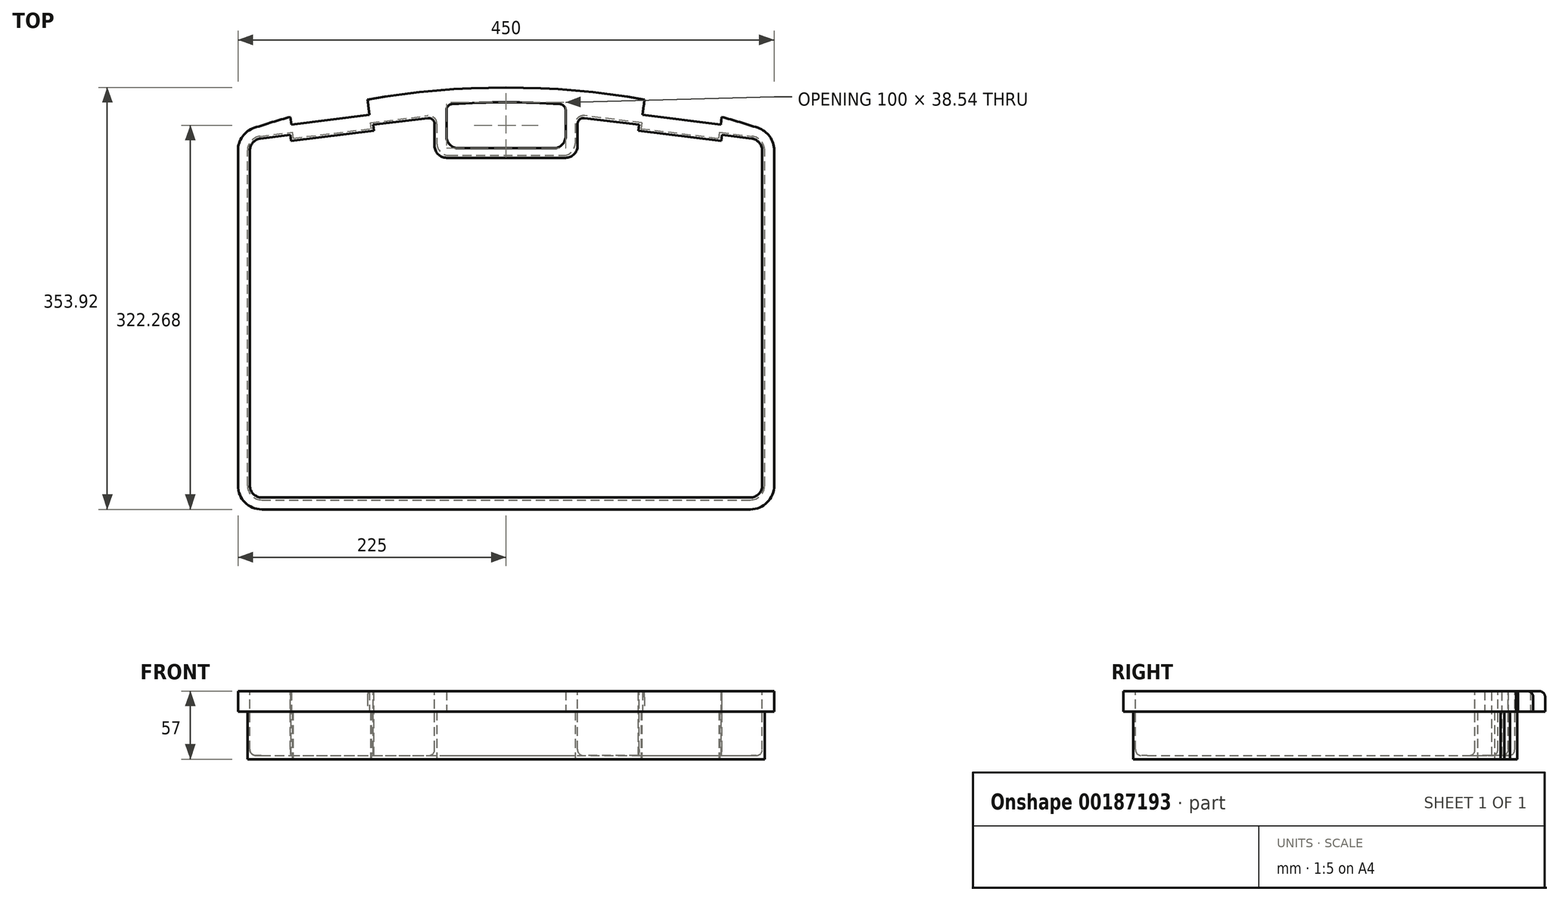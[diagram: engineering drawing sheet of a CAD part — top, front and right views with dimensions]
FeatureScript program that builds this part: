
annotation { "Feature Type Name" : "Feature", "Feature Type Description" : "" }
export const myFeature = defineFeature(function(context is Context, id is Id, definition is map)
    precondition{}
    {
        {
            var Q0;
            Q0=qCreatedBy(makeId("Top.planeOp"),FACE);
            var sketch = newSketch(context, id + "F0", { "sketchPlane" : qUnion([Q0])});
            skLineSegment(sketch, "E0.bottom", {"start": v(10, 0) * mm, "end": v(420, 0) * mm});
            skLineSegment(sketch, "E1.top", {"start": v(165, 285) * mm, "end": v(265, 285) * mm});
            skLineSegment(sketch, "E1.left", {"start": v(155, 313.35) * mm, "end": v(155, 295) * mm});
            skLineSegment(sketch, "E1.right", {"start": v(275, 313.35) * mm, "end": v(275, 295) * mm});
            skLineSegment(sketch, "E2", {"start": v(0, 10) * mm, "end": v(0, 291.15) * mm});
            skLineSegment(sketch, "E3", {"start": v(430, 10) * mm, "end": v(430, 291.15) * mm});
            skLineSegment(sketch, "E4", {"start": v(33.9, 304.16) * mm, "end": v(34.51, 299.2) * mm});
            skLineSegment(sketch, "E5", {"start": v(34.51, 299.2) * mm, "end": v(104, 307.71) * mm});
            skLineSegment(sketch, "E6", {"start": v(104, 307.71) * mm, "end": v(103.39, 312.67) * mm});
            skLineSegment(sketch, "E7", {"start": v(326.61, 312.67) * mm, "end": v(326, 307.71) * mm});
            skLineSegment(sketch, "E8", {"start": v(326, 307.71) * mm, "end": v(395.49, 299.2) * mm});
            skLineSegment(sketch, "E9", {"start": v(395.49, 299.2) * mm, "end": v(396.1, 304.16) * mm});
            skLineSegment(sketch, "E10", {"start": v(396.1, 304.16) * mm, "end": v(421.22, 301.08) * mm});
            skLineSegment(sketch, "E11", {"start": v(326.61, 312.67) * mm, "end": v(280.6, 318.31) * mm});
            skLineSegment(sketch, "E12", {"start": v(103.39, 312.67) * mm, "end": v(149.4, 318.31) * mm});
            skLineSegment(sketch, "E13", {"start": v(8.78, 301.08) * mm, "end": v(33.9, 304.16) * mm});
            skPoint(sketch, "E14.visualSharp", {"position": v(155, 285) * mm});
            skArc(sketch, "E14.filletArc", {"start": v(155, 295) * mm, "mid": v(157.93, 287.93) * mm, "end": v(165, 285) * mm});
            skPoint(sketch, "E15.visualSharp", {"position": v(275, 285) * mm});
            skArc(sketch, "E15.filletArc", {"start": v(265, 285) * mm, "mid": v(272.07, 287.93) * mm, "end": v(275, 295) * mm});
            skPoint(sketch, "E16.visualSharp", {"position": v(430, 300) * mm});
            skArc(sketch, "E16.filletArc", {"start": v(430, 291.15) * mm, "mid": v(427.49, 297.78) * mm, "end": v(421.22, 301.08) * mm});
            skPoint(sketch, "E17.visualSharp", {"position": v(0, 300) * mm});
            skArc(sketch, "E17.filletArc", {"start": v(8.78, 301.08) * mm, "mid": v(2.51, 297.78) * mm, "end": v(0, 291.15) * mm});
            skPoint(sketch, "E18.visualSharp", {"position": v(0, 0) * mm});
            skArc(sketch, "E18.filletArc", {"start": v(0, 10) * mm, "mid": v(2.93, 2.93) * mm, "end": v(10, 0) * mm});
            skPoint(sketch, "E19.visualSharp", {"position": v(430, 0) * mm});
            skArc(sketch, "E19.filletArc", {"start": v(420, 0) * mm, "mid": v(427.07, 2.93) * mm, "end": v(430, 10) * mm});
            skPoint(sketch, "E20.visualSharp", {"position": v(155, 319) * mm});
            skArc(sketch, "E20.filletArc", {"start": v(155, 313.35) * mm, "mid": v(153.31, 317.1) * mm, "end": v(149.4, 318.31) * mm});
            skPoint(sketch, "E21.visualSharp", {"position": v(275, 319) * mm});
            skArc(sketch, "E21.filletArc", {"start": v(280.6, 318.31) * mm, "mid": v(276.69, 317.1) * mm, "end": v(275, 313.35) * mm});
            skArc(sketch, "E22.0", {"start": v(-2, 10) * mm, "mid": v(1.51, 1.51) * mm, "end": v(10, -2) * mm});
            skLineSegment(sketch, "E22.1", {"start": v(10, -2) * mm, "end": v(420, -2) * mm});
            skArc(sketch, "E22.2", {"start": v(420, -2) * mm, "mid": v(428.49, 1.51) * mm, "end": v(432, 10) * mm});
            skLineSegment(sketch, "E22.3", {"start": v(432, 10) * mm, "end": v(432, 291.15) * mm});
            skArc(sketch, "E22.4", {"start": v(432, 291.15) * mm, "mid": v(428.99, 299.1) * mm, "end": v(421.46, 303.06) * mm});
            skLineSegment(sketch, "E22.5", {"start": v(-2, 10) * mm, "end": v(-2, 291.15) * mm});
            skLineSegment(sketch, "E22.6", {"start": v(394.35, 306.38) * mm, "end": v(421.46, 303.06) * mm});
            skLineSegment(sketch, "E22.7", {"start": v(393.74, 301.42) * mm, "end": v(394.35, 306.38) * mm});
            skLineSegment(sketch, "E22.8", {"start": v(328.23, 309.45) * mm, "end": v(393.74, 301.42) * mm});
            skLineSegment(sketch, "E22.9", {"start": v(328.84, 314.41) * mm, "end": v(328.23, 309.45) * mm});
            skLineSegment(sketch, "E22.10", {"start": v(328.84, 314.41) * mm, "end": v(280.85, 320.3) * mm});
            skArc(sketch, "E22.11", {"start": v(280.85, 320.3) * mm, "mid": v(275.36, 318.6) * mm, "end": v(273, 313.35) * mm});
            skLineSegment(sketch, "E22.12", {"start": v(36.26, 301.42) * mm, "end": v(101.77, 309.45) * mm});
            skLineSegment(sketch, "E22.13", {"start": v(35.65, 306.38) * mm, "end": v(36.26, 301.42) * mm});
            skLineSegment(sketch, "E22.14", {"start": v(8.54, 303.06) * mm, "end": v(35.65, 306.38) * mm});
            skArc(sketch, "E22.15", {"start": v(8.54, 303.06) * mm, "mid": v(1.01, 299.1) * mm, "end": v(-2, 291.15) * mm});
            skLineSegment(sketch, "E22.16", {"start": v(101.77, 309.45) * mm, "end": v(101.16, 314.41) * mm});
            skLineSegment(sketch, "E22.17", {"start": v(101.16, 314.41) * mm, "end": v(149.15, 320.3) * mm});
            skArc(sketch, "E22.18", {"start": v(157, 313.35) * mm, "mid": v(154.64, 318.6) * mm, "end": v(149.15, 320.3) * mm});
            skLineSegment(sketch, "E22.19", {"start": v(157, 313.35) * mm, "end": v(157, 297) * mm});
            skLineSegment(sketch, "E22.20", {"start": v(167, 287) * mm, "end": v(263, 287) * mm});
            skLineSegment(sketch, "E22.21", {"start": v(273, 313.35) * mm, "end": v(273, 297) * mm});
            skLineSegment(sketch, "E23.2", {"start": v(440, 10) * mm, "end": v(440, 291.15) * mm});
            skArc(sketch, "E23.3", {"start": v(420, -10) * mm, "mid": v(434.14, -4.14) * mm, "end": v(440, 10) * mm});
            skLineSegment(sketch, "E23.4", {"start": v(10, -10) * mm, "end": v(420, -10) * mm});
            skLineSegment(sketch, "E23.7", {"start": v(-10, 10) * mm, "end": v(-10, 291.15) * mm});
            skArc(sketch, "E23.8", {"start": v(-10, 10) * mm, "mid": v(-4.14, -4.14) * mm, "end": v(10, -10) * mm});
            skArc(sketch, "E24", {"start": v(-10, 291.15) * mm, "mid": v(-6.2, 302.88) * mm, "end": v(3.77, 310.15) * mm});
            skArc(sketch, "E25", {"start": v(440, 291.15) * mm, "mid": v(436.2, 302.88) * mm, "end": v(426.23, 310.15) * mm});
            skLineSegment(sketch, "E26", {"start": v(215, 0) * mm, "end": v(215, 285) * mm, "construction": true});
            skArc(sketch, "E27", {"start": v(3.77, 310.15) * mm, "mid": v(215, 343.92) * mm, "end": v(426.23, 310.15) * mm});
            skPoint(sketch, "E28.visualSharp", {"position": v(157, 287) * mm});
            skArc(sketch, "E28.filletArc", {"start": v(157, 297) * mm, "mid": v(159.93, 289.93) * mm, "end": v(167, 287) * mm});
            skPoint(sketch, "E29.visualSharp", {"position": v(273, 287) * mm});
            skArc(sketch, "E29.filletArc", {"start": v(263, 287) * mm, "mid": v(270.07, 289.93) * mm, "end": v(273, 297) * mm});
            skLineSegment(sketch, "E30.top", {"start": v(175, 293) * mm, "end": v(255, 293) * mm});
            skLineSegment(sketch, "E30.left", {"start": v(165, 325) * mm, "end": v(165, 303) * mm});
            skLineSegment(sketch, "E30.right", {"start": v(265, 325) * mm, "end": v(265, 303) * mm});
            skPoint(sketch, "E31.visualSharp", {"position": v(160, 292) * mm});
            skArc(sketch, "E31.filletArc", {"start": v(165, 303) * mm, "mid": v(167.93, 295.93) * mm, "end": v(175, 293) * mm});
            skPoint(sketch, "E32.visualSharp", {"position": v(270, 292) * mm});
            skArc(sketch, "E32.filletArc", {"start": v(255, 293) * mm, "mid": v(262.07, 295.93) * mm, "end": v(265, 303) * mm});
            skPoint(sketch, "E33.visualSharp", {"position": v(160, 334.8) * mm});
            skPoint(sketch, "E34.visualSharp", {"position": v(270, 334.8) * mm});
            skArc(sketch, "E35", {"start": v(165, 325) * mm, "mid": v(166.35, 328.41) * mm, "end": v(169.66, 329.99) * mm});
            skArc(sketch, "E36", {"start": v(265, 325) * mm, "mid": v(263.65, 328.41) * mm, "end": v(260.34, 329.99) * mm});
            skArc(sketch, "E37", {"start": v(169.66, 329.99) * mm, "mid": v(215, 331.54) * mm, "end": v(260.34, 329.99) * mm});
            skLineSegment(sketch, "E38", {"start": v(329.65, 320.97) * mm, "end": v(331.23, 333.87) * mm});
            skLineSegment(sketch, "E39", {"start": v(395.16, 312.94) * mm, "end": v(395.94, 319.32) * mm});
            skLineSegment(sketch, "E40", {"start": v(329.65, 320.97) * mm, "end": v(395.16, 312.94) * mm});
            skLineSegment(sketch, "E41", {"start": v(34.84, 312.94) * mm, "end": v(34.06, 319.32) * mm});
            skLineSegment(sketch, "E42", {"start": v(100.35, 320.97) * mm, "end": v(98.77, 333.87) * mm});
            skLineSegment(sketch, "E43", {"start": v(100.35, 320.97) * mm, "end": v(34.84, 312.94) * mm});
            skSolve(sketch);
        }
        {
            var Q0;
            Q0 = qSketchRegion(id + "F0", true);
            var Q1;
            Q1=makeQuery(id+"F0.imprint","IMPRINT",FACE,{"disambiguationData":[TD([[makeQuery(id+"F0.imprint","IMPRINT",EDGE,{"derivedFrom":sQuery(id+"F0.wireOp",EDGE,"E0.bottom")}),1.0]])]});
            var Q2;
            Q2=makeQuery(id+"F0.imprint","IMPRINT",FACE,{"disambiguationData":[TD([[makeQuery(id+"F0.imprint","IMPRINT",EDGE,{"derivedFrom":sQuery(id+"F0.wireOp",EDGE,"E0.bottom")}),-1.0]])]});
            extrude(context, id + "F1", {"entities" : qUnion([Q0, Q1, Q2]), "depth" : 57 * mm});
        }
        {
            var Q0;
            Q0=makeQuery(id+"F0.imprint","IMPRINT",FACE,{"disambiguationData":[TD([[makeQuery(id+"F0.imprint","IMPRINT",EDGE,{"derivedFrom":sQuery(id+"F0.wireOp",EDGE,"E0.bottom")}),1.0]])]});
            extrude(context, id + "F2", {"entities" : qUnion([Q0]), "operationType" : NewBodyOperationType.ADD, "depth" : 80 * mm});
        }
        {
            var Q0;
            Q0=makeQuery(id+"F2.opExtrude","CAP_FACE",FACE,{"disambiguationData":[OSD([sQuery(id+"F0.wireOp",EDGE,"E0.bottom"),sQuery(id+"F0.wireOp",EDGE,"E1.top"),sQuery(id+"F0.wireOp",EDGE,"E1.left"),sQuery(id+"F0.wireOp",EDGE,"E1.right"),sQuery(id+"F0.wireOp",EDGE,"E2"),sQuery(id+"F0.wireOp",EDGE,"E3"),sQuery(id+"F0.wireOp",EDGE,"E4"),sQuery(id+"F0.wireOp",EDGE,"E5"),sQuery(id+"F0.wireOp",EDGE,"E6"),sQuery(id+"F0.wireOp",EDGE,"E7"),sQuery(id+"F0.wireOp",EDGE,"E8"),sQuery(id+"F0.wireOp",EDGE,"E9"),sQuery(id+"F0.wireOp",EDGE,"E10"),sQuery(id+"F0.wireOp",EDGE,"E11"),sQuery(id+"F0.wireOp",EDGE,"E12"),sQuery(id+"F0.wireOp",EDGE,"E13"),sQuery(id+"F0.wireOp",EDGE,"E14.filletArc"),sQuery(id+"F0.wireOp",EDGE,"E15.filletArc"),sQuery(id+"F0.wireOp",EDGE,"E16.filletArc"),sQuery(id+"F0.wireOp",EDGE,"E17.filletArc"),sQuery(id+"F0.wireOp",EDGE,"E18.filletArc"),sQuery(id+"F0.wireOp",EDGE,"E19.filletArc"),sQuery(id+"F0.wireOp",EDGE,"E20.filletArc"),sQuery(id+"F0.wireOp",EDGE,"E21.filletArc")])],"isStart":false});
            extrude(context, id + "F3", {"entities" : qUnion([Q0]), "operationType" : NewBodyOperationType.REMOVE, "oppositeDirection" : true, "depth" : 77 * mm});
        }
        {
            var Q0;
            Q0=makeQuery(id+"F0.imprint","IMPRINT",FACE,{"disambiguationData":[TD([[makeQuery(id+"F0.imprint","IMPRINT",EDGE,{"derivedFrom":sQuery(id+"F0.wireOp",EDGE,"E22.0")}),-1.0]])]});
            extrude(context, id + "F4", {"entities" : qUnion([Q0]), "operationType" : NewBodyOperationType.REMOVE, "depth" : 40 * mm});
        }
        {
            var Q0;
            {var subQ0=sQuery(id+"F0.wireOp",EDGE,"E41");Q0=makeQuery(id+"F0.imprint","IMPRINT",FACE,{"disambiguationData":[TD([[makeQuery(id+"F0.imprint","IMPRINT",EDGE,{"derivedFrom":subQ0}),-1.0]])]});}
            var Q1;
            {var subQ0=sQuery(id+"F0.wireOp",EDGE,"E38");Q1=makeQuery(id+"F0.imprint","IMPRINT",FACE,{"disambiguationData":[TD([[makeQuery(id+"F0.imprint","IMPRINT",EDGE,{"derivedFrom":subQ0}),-1.0]])]});}
            extrude(context, id + "F5", {"entities" : qUnion([Q0, Q1]), "operationType" : NewBodyOperationType.REMOVE, "endBound" : BoundingType.THROUGH_ALL, "depth" : 25 * mm});
        }
        {
            var Q0;
            Q0=makeQuery(id+"F4.boolean.opBoolean","COPY",EDGE,{"derivedFrom":makeQuery(id+"F4.opExtrude","CAP_EDGE",EDGE,{"disambiguationData":[OSD([sQuery(id+"F0.wireOp",EDGE,"E23.7")])],"isStart":false})});
            var Q1;
            {var subQ0=sQuery(id+"F0.wireOp",EDGE,"E27");Q1=makeQuery(id+"F4.boolean.opBoolean","COPY",EDGE,{"derivedFrom":makeQuery(id+"F4.opExtrude","CAP_EDGE",EDGE,{"disambiguationData":[OSD([subQ0]),TDD([makeQuery(id+"F0.imprint","IMPRINT",EDGE,{"disambiguationData":[TD([[makeQuery(id+"F0.imprint","INTERSECT",VERTEX,{"derivedFrom":[subQ0,sQuery(id+"F0.wireOp",EDGE,"E38")]}),1.0]])],"derivedFrom":subQ0})])],"isStart":false})});}
            var Q2;
            {var subQ0=sQuery(id+"F0.wireOp",EDGE,"E27");Q2=makeQuery(id+"F5.boolean.opBoolean","SPLIT",EDGE,{"disambiguationData":[TD([makeQuery(id+"F5.opExtrude","SWEPT_FACE",FACE,{"disambiguationData":[OSD([sQuery(id+"F0.wireOp",EDGE,"E38")])]})])],"derivedFrom":makeQuery(id+"F1.opExtrude","CAP_EDGE",EDGE,{"disambiguationData":[OSD([subQ0])],"isStart":false})});}
            var Q3;
            Q3=makeQuery(id+"F4.boolean.opBoolean","COPY",EDGE,{"derivedFrom":makeQuery(id+"F4.opExtrude","CAP_EDGE",EDGE,{"disambiguationData":[OSD([sQuery(id+"F0.wireOp",EDGE,"E37")])],"isStart":false})});
            var Q4;
            Q4=makeQuery(id+"F4.boolean.opBoolean","COPY",EDGE,{"derivedFrom":makeQuery(id+"F4.opExtrude","CAP_EDGE",EDGE,{"disambiguationData":[OSD([sQuery(id+"F0.wireOp",EDGE,"E22.3")])],"isStart":true})});
            var Q5;
            Q5=makeQuery(id+"F4.boolean.opBoolean","COPY",EDGE,{"derivedFrom":makeQuery(id+"F4.opExtrude","CAP_EDGE",EDGE,{"disambiguationData":[OSD([sQuery(id+"F0.wireOp",EDGE,"E22.20")])],"isStart":true})});
            var Q6;
            Q6=makeQuery(id+"F3.boolean.opBoolean","COPY",EDGE,{"derivedFrom":makeQuery(id+"F3.opExtrude","CAP_EDGE",EDGE,{"disambiguationData":[OSD([sQuery(id+"F0.wireOp",EDGE,"E13")])],"isStart":false})});
            var Q7;
            Q7=makeQuery(id+"F3.boolean.opBoolean","COPY",EDGE,{"derivedFrom":makeQuery(id+"F3.opExtrude","CAP_EDGE",EDGE,{"disambiguationData":[OSD([sQuery(id+"F0.wireOp",EDGE,"E12")])],"isStart":false})});
            fillet(context, id + "F6", {"entities" : qUnion([Q0, Q1, Q2, Q3, Q4, Q5, Q6, Q7]), "radius" : 5 * mm, "tangentPropagation" : true, "allowEdgeOverflow" : false});
        }
    });
